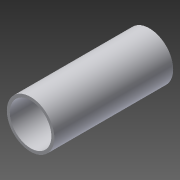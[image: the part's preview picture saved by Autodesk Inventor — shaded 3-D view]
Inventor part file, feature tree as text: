
AUTODESK INVENTOR PART (.ipt)
format: ipt  version: 2015 (Build 190159000, 159)  size: 96,768 bytes
history: native  units: mm
features: other x1, extrude x1, shell x1, sketch x1
ambient origin geometry x8: Origin, YZ Plane, XZ Plane, XY Plane, X Axis, Y Axis, Z Axis, Center Point
bodies: Body1 (feature_tree)
feature tree (4):
  other  "Bryła1"
  extrude  "Wyciągnięcie proste1"  Depth=32.0mm
  shell  "Skorupa1"  Thickness=80.0mm
  sketch  "Szkic1"
